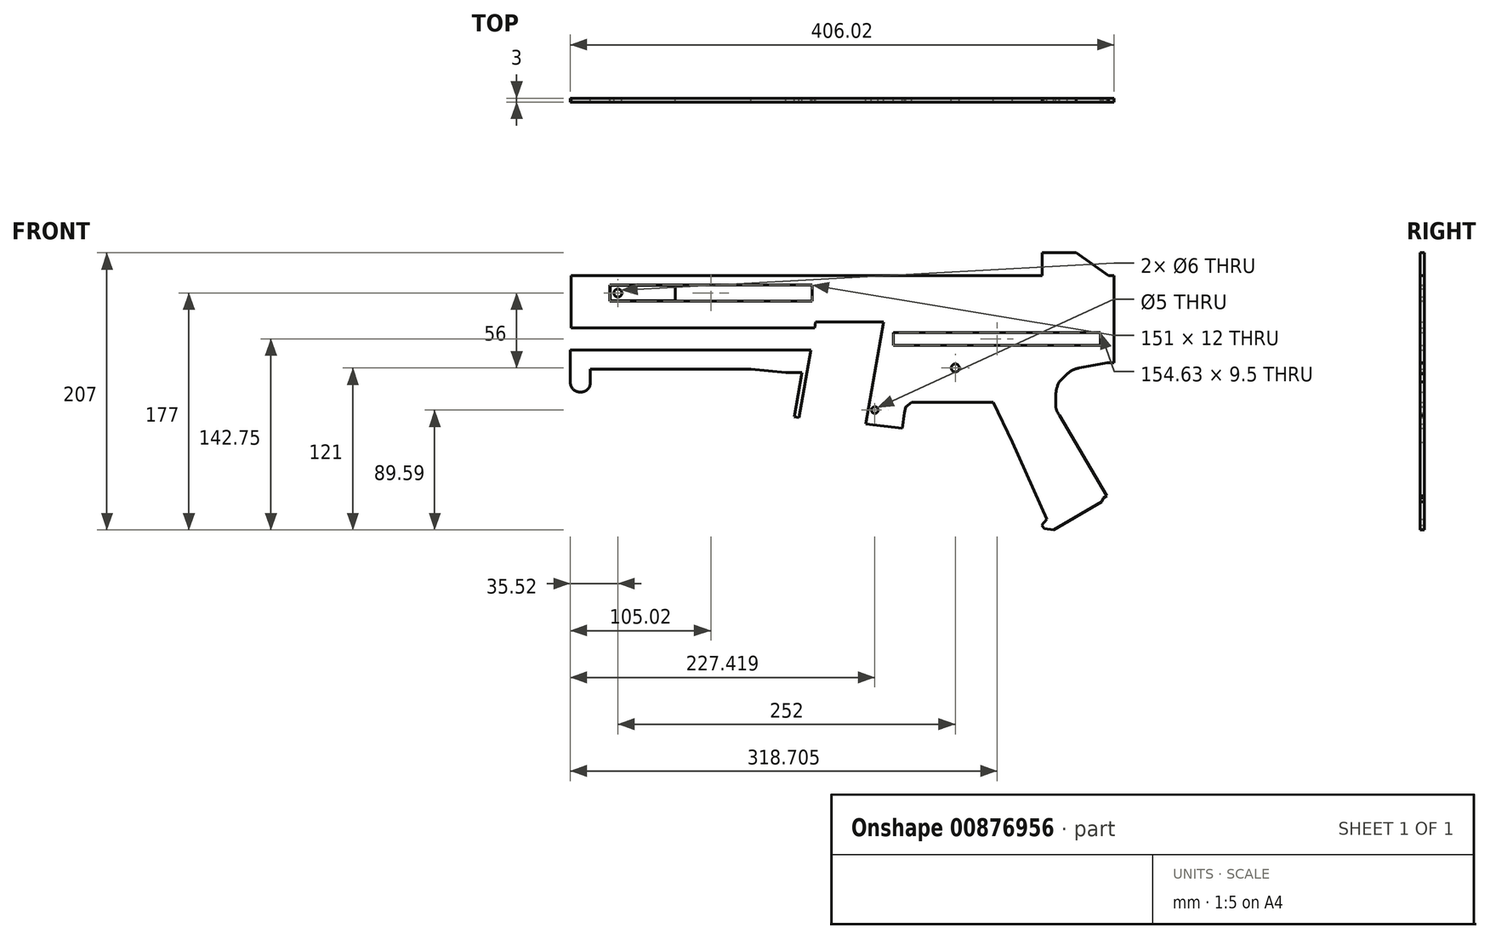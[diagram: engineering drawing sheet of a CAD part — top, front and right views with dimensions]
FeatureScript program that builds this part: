
annotation { "Feature Type Name" : "Feature", "Feature Type Description" : "" }
export const myFeature = defineFeature(function(context is Context, id is Id, definition is map)
    precondition{}
    {
        {
            var Q0;
            Q0=qCreatedBy(makeId("Front.planeOp"),FACE);
            var sketch = newSketch(context, id + "F0", { "sketchPlane" : qUnion([Q0])});
            skLineSegment(sketch, "E0", {"start": v(53.5, -65) * mm, "end": v(53.5, 0) * mm});
            skLineSegment(sketch, "E1", {"start": v(0, 0) * mm, "end": v(0, 17) * mm});
            skLineSegment(sketch, "E2", {"start": v(0, 17) * mm, "end": v(25.27, 17) * mm});
            skPoint(sketch, "E3.visualSharp", {"position": v(0, 17) * mm});
            skPoint(sketch, "E4.visualSharp", {"position": v(25.27, 17) * mm});
            skPoint(sketch, "E5.visualSharp", {"position": v(53.5, 0) * mm});
            skPoint(sketch, "E6.visualSharp", {"position": v(0, 0) * mm});
            skLineSegment(sketch, "E7", {"start": v(53.5, -65) * mm, "end": v(48.5, -65) * mm});
            skLineSegment(sketch, "E8", {"start": v(48.5, -65) * mm, "end": v(27.5, -69) * mm});
            skLineSegment(sketch, "E9", {"start": v(18.5, -73.5) * mm, "end": v(12.5, -79.5) * mm});
            skLineSegment(sketch, "E10", {"start": v(10, -90.5) * mm, "end": v(10, -96.5) * mm});
            skLineSegment(sketch, "E11", {"start": v(13, -104.5) * mm, "end": v(48, -164.5) * mm});
            skLineSegment(sketch, "E12", {"start": v(48, -164.5) * mm, "end": v(45.5, -166) * mm});
            skLineSegment(sketch, "E13", {"start": v(45.5, -166) * mm, "end": v(44.5, -169) * mm});
            skLineSegment(sketch, "E14", {"start": v(44.5, -169) * mm, "end": v(8.5, -190) * mm});
            skLineSegment(sketch, "E15", {"start": v(8.5, -190) * mm, "end": v(1.5, -189) * mm});
            skLineSegment(sketch, "E16", {"start": v(1.5, -189) * mm, "end": v(-0.5, -186.5) * mm});
            skLineSegment(sketch, "E17", {"start": v(-0.5, -186.5) * mm, "end": v(3.5, -182) * mm});
            skLineSegment(sketch, "E18", {"start": v(-104.53, -114) * mm, "end": v(-131.94, -110.95) * mm});
            skArc(sketch, "E19", {"start": v(10, -90.5) * mm, "mid": v(10.63, -84.86) * mm, "end": v(12.5, -79.5) * mm});
            skArc(sketch, "E20", {"start": v(27.5, -69) * mm, "mid": v(22.69, -70.63) * mm, "end": v(18.5, -73.5) * mm});
            skArc(sketch, "E21", {"start": v(10, -96.5) * mm, "mid": v(10.77, -100.77) * mm, "end": v(13, -104.5) * mm});
            skLineSegment(sketch, "E22", {"start": v(0, 0) * mm, "end": v(-352, 0) * mm});
            skLineSegment(sketch, "E23", {"start": v(-345.52, -87) * mm, "end": v(-344.52, -87) * mm});
            skLineSegment(sketch, "E24", {"start": v(-337.52, -80) * mm, "end": v(-337.52, -70) * mm});
            skLineSegment(sketch, "E25", {"start": v(-337.52, -70) * mm, "end": v(-217.52, -70) * mm});
            skLineSegment(sketch, "E26", {"start": v(-217.52, -70) * mm, "end": v(-191.52, -72.5) * mm});
            skLineSegment(sketch, "E27", {"start": v(-191.52, -72.5) * mm, "end": v(-179.52, -72.5) * mm});
            skLineSegment(sketch, "E28", {"start": v(-179.52, -72.5) * mm, "end": v(-185.34, -105.5) * mm});
            skLineSegment(sketch, "E29", {"start": v(-352.52, -80) * mm, "end": v(-352.52, -55.5) * mm});
            skLineSegment(sketch, "E30", {"start": v(-352, 0) * mm, "end": v(-352, -39) * mm});
            skLineSegment(sketch, "E31", {"start": v(-103, -102.5) * mm, "end": v(-102, -98) * mm});
            skLineSegment(sketch, "E32", {"start": v(-102, -98) * mm, "end": v(-97.5, -94.5) * mm});
            skLineSegment(sketch, "E33", {"start": v(-181.84, -106) * mm, "end": v(-185.34, -105.5) * mm});
            skLineSegment(sketch, "E34", {"start": v(-181.84, -106) * mm, "end": v(-172.93, -55.5) * mm});
            skLineSegment(sketch, "E35", {"start": v(-172.93, -55.5) * mm, "end": v(-352.52, -55.5) * mm});
            skLineSegment(sketch, "E36", {"start": v(-131.94, -110.95) * mm, "end": v(-121.55, -52) * mm});
            skPoint(sketch, "E37", {"position": v(-317, -13) * mm});
            skPoint(sketch, "E38", {"position": v(-215, -13) * mm});
            skLineSegment(sketch, "E39", {"start": v(-97.5, -94.5) * mm, "end": v(-36.5, -94.5) * mm});
            skPoint(sketch, "E40.visualSharp", {"position": v(-352.52, -87) * mm});
            skArc(sketch, "E40.filletArc", {"start": v(-352.52, -80) * mm, "mid": v(-350.47, -84.95) * mm, "end": v(-345.52, -87) * mm});
            skPoint(sketch, "E41.visualSharp", {"position": v(-337.52, -87) * mm});
            skArc(sketch, "E41.filletArc", {"start": v(-344.52, -87) * mm, "mid": v(-339.57, -84.95) * mm, "end": v(-337.52, -80) * mm});
            skPoint(sketch, "E42", {"position": v(-323, -7) * mm});
            skPoint(sketch, "E43", {"position": v(-209, -7) * mm});
            skLineSegment(sketch, "E44.bottom", {"start": v(-323, -7) * mm, "end": v(-172, -7) * mm});
            skLineSegment(sketch, "E44.top", {"start": v(-323, -19) * mm, "end": v(-172, -19) * mm});
            skLineSegment(sketch, "E44.left", {"start": v(-323, -7) * mm, "end": v(-323, -19) * mm});
            skLineSegment(sketch, "E44.right", {"start": v(-172, -7) * mm, "end": v(-172, -19) * mm});
            skPoint(sketch, "E45", {"position": v(-121.16, -2.5) * mm});
            skLineSegment(sketch, "E46", {"start": v(-119.21, -38.77) * mm, "end": v(-118.5, -34.77) * mm});
            skLineSegment(sketch, "E47", {"start": v(-170.03, -39) * mm, "end": v(-169.28, -34.77) * mm});
            skLineSegment(sketch, "E48", {"start": v(-169.28, -34.77) * mm, "end": v(-118.5, -34.77) * mm});
            skLineSegment(sketch, "E49", {"start": v(-352, -39) * mm, "end": v(-170.03, -39) * mm});
            skLineSegment(sketch, "E50", {"start": v(-121.55, -52) * mm, "end": v(-119.21, -38.77) * mm});
            skLineSegment(sketch, "E51", {"start": v(-104.53, -114) * mm, "end": v(-103, -102.5) * mm});
            skLineSegment(sketch, "E52", {"start": v(3.5, -182) * mm, "end": v(-22.5, -124.5) * mm});
            skLineSegment(sketch, "E53", {"start": v(-22.5, -124.5) * mm, "end": v(-36.5, -94.5) * mm});
            skCircle(sketch, "E54", {"center": v(-65, -69) * mm, "radius": 3 * mm});
            skCircle(sketch, "E55", {"center": v(-125.1, -100.4) * mm, "radius": 2.5 * mm});
            skLineSegment(sketch, "E56", {"start": v(25.27, 17) * mm, "end": v(49.5, 0) * mm});
            skLineSegment(sketch, "E57", {"start": v(49.5, 0) * mm, "end": v(53.5, 0) * mm});
            skPoint(sketch, "E58", {"position": v(-323, -13) * mm});
            skCircle(sketch, "E59", {"center": v(-317, -13) * mm, "radius": 3 * mm});
            skPoint(sketch, "E60", {"position": v(-314, -13) * mm});
            skLineSegment(sketch, "E61.bottom", {"start": v(-322.75, -7.25) * mm, "end": v(-274, -7.25) * mm});
            skLineSegment(sketch, "E61.top", {"start": v(-322.75, -18.75) * mm, "end": v(-274, -18.75) * mm});
            skLineSegment(sketch, "E61.left", {"start": v(-322.75, -7.25) * mm, "end": v(-322.75, -18.75) * mm});
            skLineSegment(sketch, "E61.right", {"start": v(-274, -7.25) * mm, "end": v(-274, -18.75) * mm});
            skLineSegment(sketch, "E62.bottom", {"start": v(-111.13, -42.5) * mm, "end": v(43.5, -42.5) * mm});
            skLineSegment(sketch, "E62.top", {"start": v(-111.13, -52) * mm, "end": v(43.5, -52) * mm});
            skLineSegment(sketch, "E62.left", {"start": v(-111.13, -42.5) * mm, "end": v(-111.13, -52) * mm});
            skLineSegment(sketch, "E62.right", {"start": v(43.5, -42.5) * mm, "end": v(43.5, -52) * mm});
            skPoint(sketch, "E63", {"position": v(43.5, -47.25) * mm});
            skSolve(sketch);
        }
        {
            var Q0;
            Q0=qSketchRegion(id+"F0",true);
            var Q1;
            Q1=makeQuery(id+"F0.imprint","IMPRINT",FACE,{"disambiguationData":[TD([[makeQuery(id+"F0.imprint","IMPRINT",EDGE,{"derivedFrom":sQuery(id+"F0.wireOp",EDGE,"7KHTMWfU-3Zso-w6jU-E75I-gNLATLITgT0v.bottom")}),-1.0]])]});
            var Q2;
            Q2=makeQuery(id+"F0.imprint","IMPRINT",FACE,{"disambiguationData":[TD([[makeQuery(id+"F0.imprint","IMPRINT",EDGE,{"derivedFrom":sQuery(id+"F0.wireOp",EDGE,"h5b3wBjq-2nQV-NM1d-5vbp-s6v93ooiL6zY.bottom")}),-1.0]])]});
            var Q3;
            Q3=makeQuery(id+"F0.imprint","IMPRINT",FACE,{"disambiguationData":[TD([[makeQuery(id+"F0.imprint","IMPRINT",EDGE,{"derivedFrom":sQuery(id+"F0.wireOp",EDGE,"E59")}),-1.0]])]});
            extrude(context, id + "F1", {"entities" : qUnion([Q0, Q1, Q2, Q3]), "depth" : 3 * mm, "offsetDistance" : 25 * mm});
        }
    });
